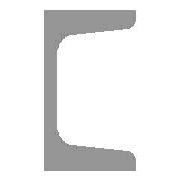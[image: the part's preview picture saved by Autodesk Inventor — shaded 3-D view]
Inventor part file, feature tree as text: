
AUTODESK INVENTOR PART (.ipt)
format: ipt  version: 2019 (Build 230136000, 136)  size: 148,992 bytes
history: native  units: mm (DEFAULTED — no unit token found)
features: other x4, sketch x3, plane x1
ambient origin geometry x8: Origin, YZ Plane, XZ Plane, XY Plane, X Axis, Y Axis, Z Axis, Center Point
bodies: Solid1 (feature_tree), Body (feature_tree)
feature tree (8):
  parser-record x1  (decoder bookkeeping rows leaked as tree rows — omitted from the tree; the rows remain in map.json)
  other  "Driven Length"
  other  "Start plane"
  other  "End plane"
  sketch  "Sketch5"  dims[d2=38.0mm d3=7.0mm d4=19.0mm d5=1.52mm d6=107.907368mm d7=0.0mm d23=7.0mm d24=3.5mm d25=0.0mm d26=-0.0mm d27=107.907368mm d28=90.0deg d29=107.907368mm d30=50.0mm d31=30.0mm d32=5.0mm d33=12.169223mm d34=25.830777mm]
  sketch  "Sketch3"  dims[d0=5.0mm]
  plane  "Work Plane3"
  sketch  "Sketch4"  dims[d1=25.0mm]
